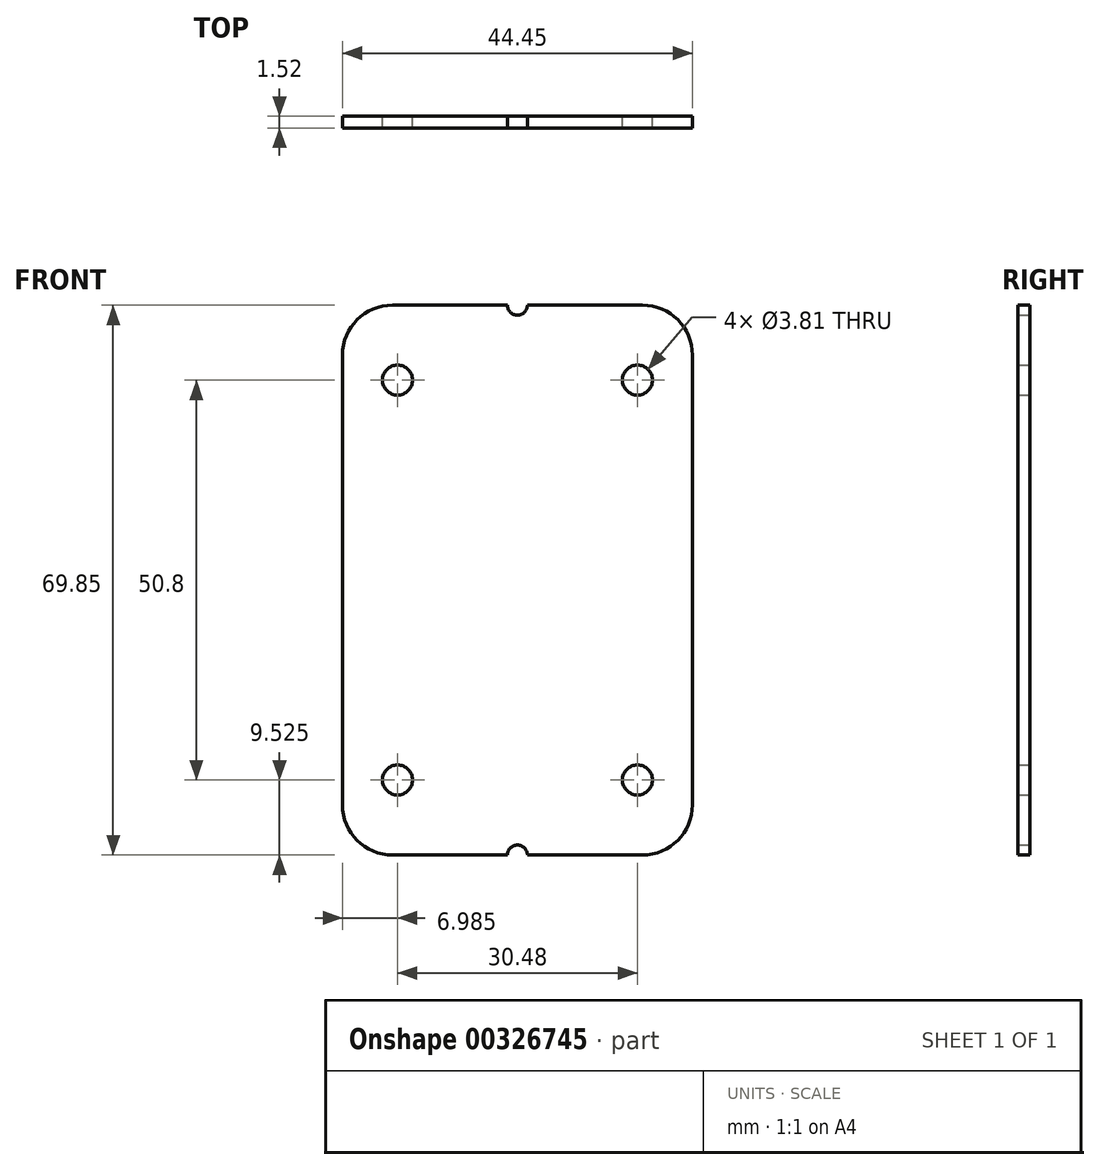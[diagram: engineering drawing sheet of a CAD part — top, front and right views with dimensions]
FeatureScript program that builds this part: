
annotation { "Feature Type Name" : "Feature", "Feature Type Description" : "" }
export const myFeature = defineFeature(function(context is Context, id is Id, definition is map)
    precondition{}
    {
        {
            var Q0;
            Q0=qCreatedBy(makeId("Front.planeOp"),FACE);
            var sketch = newSketch(context, id + "F0", { "sketchPlane" : qUnion([Q0])});
            skLineSegment(sketch, "E0.bottom", {"start": v(6.35, 0) * mm, "end": v(20.96, 0) * mm});
            skLineSegment(sketch, "E0.top", {"start": v(6.35, 69.85) * mm, "end": v(20.95, 69.85) * mm});
            skLineSegment(sketch, "E0.left", {"start": v(0, 6.35) * mm, "end": v(0, 63.5) * mm});
            skLineSegment(sketch, "E0.right", {"start": v(44.45, 6.35) * mm, "end": v(44.45, 63.5) * mm});
            skCircle(sketch, "E1", {"center": v(6.98, 60.33) * mm, "radius": 1.9 * mm});
            skCircle(sketch, "E2.MirrorC", {"center": v(37.46, 60.33) * mm, "radius": 1.9 * mm});
            skCircle(sketch, "E3.MirrorC", {"center": v(6.98, 9.52) * mm, "radius": 1.9 * mm});
            skCircle(sketch, "E4.MirrorC", {"center": v(37.46, 9.52) * mm, "radius": 1.9 * mm});
            skPoint(sketch, "E5.visualSharp", {"position": v(0, 69.85) * mm});
            skArc(sketch, "E5.filletArc", {"start": v(6.35, 69.85) * mm, "mid": v(1.86, 68) * mm, "end": v(0, 63.5) * mm});
            skPoint(sketch, "E6.visualSharp", {"position": v(44.45, 69.85) * mm});
            skArc(sketch, "E6.filletArc", {"start": v(44.45, 63.5) * mm, "mid": v(42.6, 68) * mm, "end": v(38.1, 69.85) * mm});
            skPoint(sketch, "E7.visualSharp", {"position": v(0, 0) * mm});
            skArc(sketch, "E7.filletArc", {"start": v(0, 6.35) * mm, "mid": v(1.86, 1.86) * mm, "end": v(6.35, 0) * mm});
            skPoint(sketch, "E8.visualSharp", {"position": v(44.45, 0) * mm});
            skArc(sketch, "E8.filletArc", {"start": v(38.1, 0) * mm, "mid": v(42.6, 1.86) * mm, "end": v(44.45, 6.35) * mm});
            skArc(sketch, "E9", {"start": v(20.95, 69.85) * mm, "mid": v(22.22, 68.58) * mm, "end": v(23.5, 69.85) * mm});
            skArc(sketch, "E10", {"start": v(23.5, 0) * mm, "mid": v(22.23, 1.27) * mm, "end": v(20.96, 0) * mm});
            skLineSegment(sketch, "E11.trimOffspring", {"start": v(23.5, 69.85) * mm, "end": v(38.1, 69.85) * mm});
            skLineSegment(sketch, "E12.trimOffspring", {"start": v(23.5, 0) * mm, "end": v(38.1, 0) * mm});
            skLineSegment(sketch, "E13", {"start": v(6.35, 0) * mm, "end": v(6.35, -18.86) * mm});
            skSolve(sketch);
        }
        {
            var Q0;
            Q0 = qSketchRegion(id + "F0", true);
            extrude(context, id + "F1", {"entities" : qUnion([Q0]), "depth" : 1.52 * mm});
        }
    });
